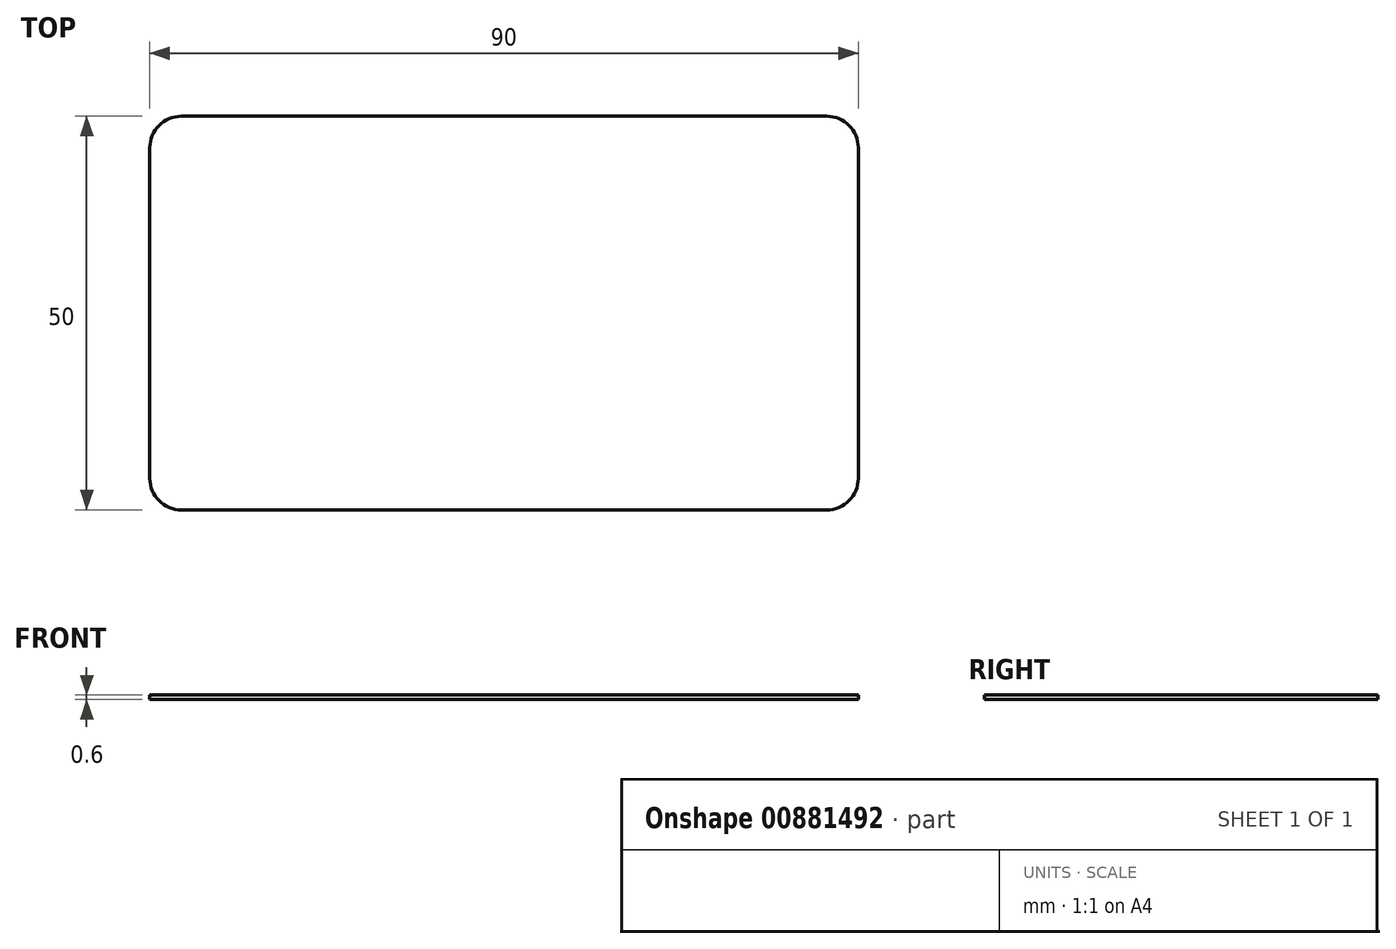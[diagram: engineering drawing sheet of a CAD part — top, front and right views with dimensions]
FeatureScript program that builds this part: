
annotation { "Feature Type Name" : "Feature", "Feature Type Description" : "" }
export const myFeature = defineFeature(function(context is Context, id is Id, definition is map)
    precondition{}
    {
        {
            var Q0;
            Q0=qCreatedBy(makeId("Top.planeOp"),FACE);
            var sketch = newSketch(context, id + "F0", { "sketchPlane" : qUnion([Q0])});
            skLineSegment(sketch, "E0.bottom", {"start": v(-45, 25) * mm, "end": v(45, 25) * mm});
            skLineSegment(sketch, "E0.left", {"start": v(-45, 25) * mm, "end": v(-45, -25) * mm});
            skText(sketch, "E1", { "text": "Jakub Mašát", "fontName": "OpenSans-Bold.ttf"});
            skText(sketch, "E2", { "text": "<email>", "fontName": "OpenSans-Regular.ttf"});
            skText(sketch, "E3", { "text": "<phone>", "fontName": "OpenSans-Regular.ttf"});
            skText(sketch, "E4", { "text": "3D Tisk / Prototypování\nModelování / Konzultace", "fontName": "OpenSans-Regular.ttf"});
            const initialGuessF0  = {"E1": [-0.03497, 0.012, 1, 0, 0.008], "E2": [-0.03546, 0.004, 1, 0, 0.004], "E3": [-0.03356, -0.005, 1, 0, 0.006], "E4": [-0.03984, -0.013, 1, 0, 0.005]};
            skSetInitialGuess(sketch, initialGuessF0);
            skSolve(sketch);
        }
        {
            var Q0;
            Q0=qCreatedBy(makeId("Top.planeOp"),FACE);
            var sketch = newSketch(context, id + "F1", { "sketchPlane" : qUnion([Q0])});
            skLineSegment(sketch, "E5.bottom", {"start": v(-45, 25) * mm, "end": v(45, 25) * mm});
            skLineSegment(sketch, "E5.top", {"start": v(-45, -25) * mm, "end": v(45, -25) * mm});
            skLineSegment(sketch, "E5.left", {"start": v(-45, 25) * mm, "end": v(-45, -25) * mm});
            skLineSegment(sketch, "E5.right", {"start": v(45, 25) * mm, "end": v(45, -25) * mm});
            skSolve(sketch);
        }
        {
            var Q0;
            Q0 = qSketchRegion(id + "F1", true);
            extrude(context, id + "F2", {"entities" : qUnion([Q0]), "depth" : 0.6 * mm, "offsetDistance" : 25 * mm});
        }
        {
            var Q0;
            Q0=makeQuery(id+"F2.opExtrude","SWEPT_EDGE",EDGE,{"disambiguationData":[OSD([sQuery(id+"F1.wireOp",EDGE,"E5.bottom"),sQuery(id+"F1.wireOp",EDGE,"E5.left")])]});
            var Q1;
            Q1=makeQuery(id+"F2.opExtrude","SWEPT_EDGE",EDGE,{"disambiguationData":[OSD([sQuery(id+"F1.wireOp",EDGE,"E5.bottom"),sQuery(id+"F1.wireOp",EDGE,"E5.right")])]});
            var Q2;
            Q2=makeQuery(id+"F2.opExtrude","SWEPT_EDGE",EDGE,{"disambiguationData":[OSD([sQuery(id+"F1.wireOp",EDGE,"E5.top"),sQuery(id+"F1.wireOp",EDGE,"E5.right")])]});
            var Q3;
            Q3=makeQuery(id+"F2.opExtrude","SWEPT_EDGE",EDGE,{"disambiguationData":[OSD([sQuery(id+"F1.wireOp",EDGE,"E5.top"),sQuery(id+"F1.wireOp",EDGE,"E5.left")])]});
            fillet(context, id + "F3", {"entities" : qUnion([Q0, Q1, Q2, Q3]), "radius" : 4 * mm, "tangentPropagation" : true, "allowEdgeOverflow" : false});
        }
    });
